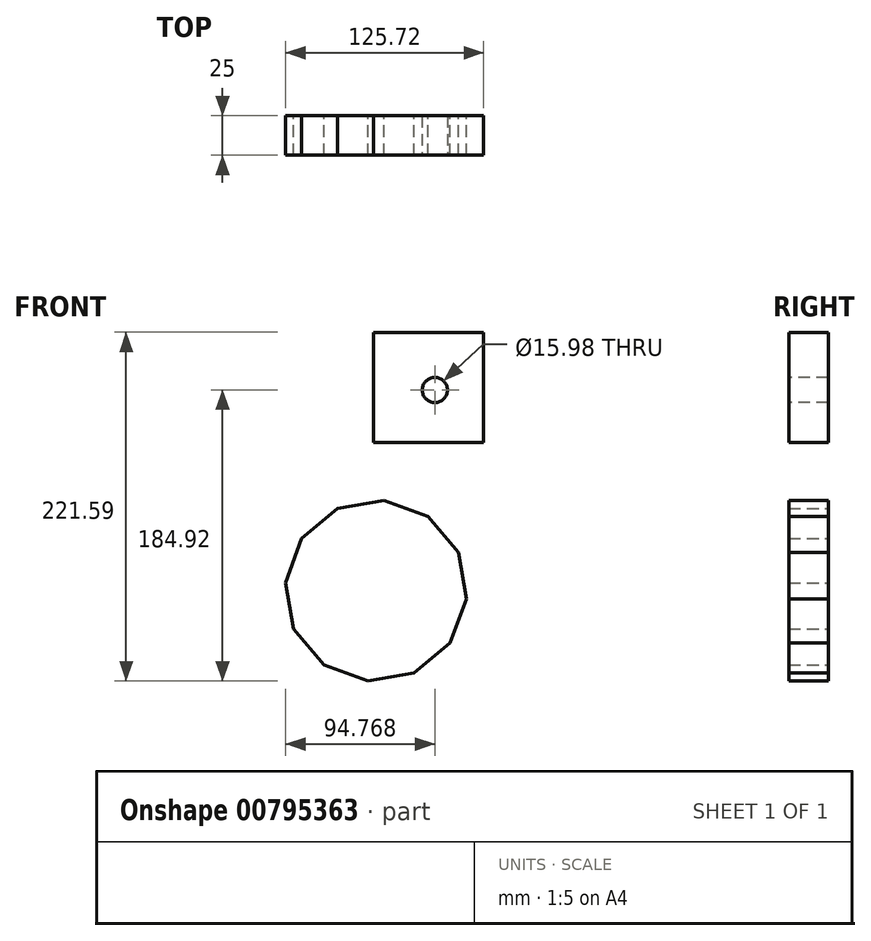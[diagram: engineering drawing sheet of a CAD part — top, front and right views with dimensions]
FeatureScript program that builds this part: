
annotation { "Feature Type Name" : "Feature", "Feature Type Description" : "" }
export const myFeature = defineFeature(function(context is Context, id is Id, definition is map)
    precondition{}
    {
        {
            var Q0;
            Q0=qCreatedBy(makeId("Front.planeOp"),FACE);
            var sketch = newSketch(context, id + "F0", { "sketchPlane" : qUnion([Q0])});
            skLineSegment(sketch, "E0.bottom", {"start": v(-281.43, 36.67) * mm, "end": v(-211.43, 36.67) * mm});
            skLineSegment(sketch, "E0.top", {"start": v(-281.43, -33.33) * mm, "end": v(-211.43, -33.33) * mm});
            skLineSegment(sketch, "E0.left", {"start": v(-281.43, 36.67) * mm, "end": v(-281.43, -33.33) * mm});
            skLineSegment(sketch, "E0.right", {"start": v(-211.43, 36.67) * mm, "end": v(-211.43, -33.33) * mm});
            skCircle(sketch, "E1", {"center": v(629.42, 23.51) * mm, "radius": 37.18 * mm});
            skSolve(sketch);
        }
        {
            var Q0;
            Q0=qCreatedBy(makeId("Front.planeOp"),FACE);
            var sketch = newSketch(context, id + "F1", { "sketchPlane" : qUnion([Q0])});
            skCircle(sketch, "E2.cCircle", {"center": v(-279.74, -127.51) * mm, "radius": 55.67 * mm, "construction": true});
            skLineSegment(sketch, "E2.0", {"start": v(-255.47, -179.79) * mm, "end": v(-284.86, -184.92) * mm});
            skLineSegment(sketch, "E2.1", {"start": v(-284.86, -184.92) * mm, "end": v(-312.88, -174.68) * mm});
            skLineSegment(sketch, "E2.2", {"start": v(-312.88, -174.68) * mm, "end": v(-332.02, -151.8) * mm});
            skLineSegment(sketch, "E2.3", {"start": v(-332.02, -151.8) * mm, "end": v(-337.15, -122.4) * mm});
            skLineSegment(sketch, "E2.4", {"start": v(-337.15, -122.4) * mm, "end": v(-326.9, -94.38) * mm});
            skLineSegment(sketch, "E2.5", {"start": v(-326.9, -94.38) * mm, "end": v(-304.02, -75.24) * mm});
            skLineSegment(sketch, "E2.6", {"start": v(-304.02, -75.24) * mm, "end": v(-274.63, -70.1) * mm});
            skLineSegment(sketch, "E2.7", {"start": v(-274.63, -70.1) * mm, "end": v(-246.61, -80.35) * mm});
            skLineSegment(sketch, "E2.8", {"start": v(-246.61, -80.35) * mm, "end": v(-227.47, -103.24) * mm});
            skLineSegment(sketch, "E2.9", {"start": v(-227.47, -103.24) * mm, "end": v(-222.33, -132.63) * mm});
            skLineSegment(sketch, "E2.10", {"start": v(-222.33, -132.63) * mm, "end": v(-232.58, -160.65) * mm});
            skLineSegment(sketch, "E2.11", {"start": v(-232.58, -160.65) * mm, "end": v(-255.47, -179.79) * mm});
            skPoint(sketch, "E2.0.midPoint", {"position": v(-270.16, -182.36) * mm});
            skSolve(sketch);
        }
        {
            var Q0;
            Q0=qCreatedBy(makeId("Front.planeOp"),FACE);
            var sketch = newSketch(context, id + "F2", { "sketchPlane" : qUnion([Q0])});
            skSolve(sketch);
        }
        {
            var Q0;
            Q0=makeQuery(id+"F0.imprint","IMPRINT",FACE,{"disambiguationData":[TD([[makeQuery(id+"F0.imprint","IMPRINT",EDGE,{"derivedFrom":sQuery(id+"F0.wireOp",EDGE,"E0.bottom")}),-1.0]])]});
            var Q1;
            Q1 = qSketchRegion(id + "F2", true);
            var Q2;
            Q2=makeQuery(id+"F1.imprint","IMPRINT",FACE,{"disambiguationData":[TD([[makeQuery(id+"F1.imprint","IMPRINT",EDGE,{"derivedFrom":sQuery(id+"F1.wireOp",EDGE,"E2.0")}),-1.0]])]});
            extrude(context, id + "F3", {"entities" : qUnion([Q0, Q1, Q2]), "depth" : 25 * mm, "offsetDistance" : 25 * mm});
        }
        {
            var Q0;
            Q0=makeQuery(id+"F3.opExtrude","CAP_FACE",FACE,{"disambiguationData":[OSD([sQuery(id+"F0.wireOp",EDGE,"E0.bottom"),sQuery(id+"F0.wireOp",EDGE,"E0.top"),sQuery(id+"F0.wireOp",EDGE,"E0.left"),sQuery(id+"F0.wireOp",EDGE,"E0.right")])],"isStart":false});
            var sketch = newSketch(context, id + "F4", { "sketchPlane" : qUnion([Q0])});
            skCircle(sketch, "E3", {"center": v(-242.38, 0) * mm, "radius": 8 * mm});
            skSolve(sketch);
        }
        {
            var Q0;
            Q0 = qSketchRegion(id + "F4", true);
            extrude(context, id + "F5", {"entities" : qUnion([Q0]), "operationType" : NewBodyOperationType.REMOVE, "oppositeDirection" : true, "depth" : 25 * mm, "offsetDistance" : 25 * mm});
        }
    });
